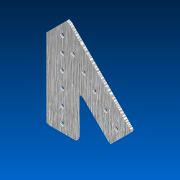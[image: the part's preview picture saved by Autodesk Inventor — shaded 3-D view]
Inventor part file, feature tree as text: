
AUTODESK INVENTOR PART (.ipt)
format: ipt  version: 2022.2 (Build 262287000, 287)  size: 152,576 bytes
history: native  units: in
note: dims shown in document units (in); Inventor stores cm internally (conversion verified against a paired STEP export)
features: extrude x1, sketch x1, other x1
ambient origin geometry x8: Origin, YZ Plane, XZ Plane, XY Plane, X Axis, Y Axis, Z Axis, Center Point
bodies: Solid1 (feature_tree)
feature tree (3):
  extrude  "Extrusion1"  TaperAngle=0.0deg  [1 undecoded]
  sketch  "Sketch1"  dims[d0=45.0deg d1=0.0in d2=0.0in]
  other  "Cut-Extrude2"
note: 1 required parameter value undecoded (feature->parameter linkage not recoverable at this tier; creation-order binding heuristic only, values carry confidence <= 0.55)
